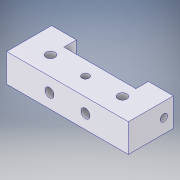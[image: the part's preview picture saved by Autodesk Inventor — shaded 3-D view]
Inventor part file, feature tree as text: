
AUTODESK INVENTOR PART (.ipt)
format: ipt  version: 2017 (Build 210142000, 142)  size: 185,344 bytes
history: native  units: in
note: dims shown in document units (in); Inventor stores cm internally (conversion verified against a paired STEP export)
features: extrude x8, sketch x8, projected_geometry x5
ambient origin geometry x8: Origin, YZ Plane, XZ Plane, XY Plane, X Axis, Y Axis, Z Axis, Center Point
bodies: Solid1 (feature_tree)
feature tree (21):
  extrude  "Extrusion1"  Depth=1.6929in
  extrude  "Extrusion2"  Depth=0.3937in
  extrude  "Extrusion3"  Depth=0.1969in TaperAngle=0.0deg
  extrude  "Extrusion4"  Depth=0.1969in
  extrude  "Extrusion5"  Depth=0.0984in
  extrude  "Extrusion6"  Depth=0.3937in TaperAngle=0.0deg
  extrude  "Extrusion7"  Depth=1.0in
  extrude  "Extrusion8"  Depth=0.625in
  sketch  "Sketch1"  dims[d0=2.4016in d1=1.6929in]
  sketch  "Sketch2"  dims[d2=0.3937in d3=0.0in d4=0.4921in]
  sketch  "Sketch3"  dims[d5=0.0984in d6=0.1969in d7=0.0in]
  projected_geometry  "Projected Loop1"
  sketch  "Sketch4"  dims[d8=0.1969in d9=0.0in d10=0.25in]
  sketch  "Sketch5"  dims[d11=0.25in d12=0.0984in]
  projected_geometry  "Projected Loop2"
  sketch  "Sketch6"  dims[d13=0.0984in d14=0.3937in d15=0.0in]
  projected_geometry  "Projected Loop3"
  sketch  "Sketch7"  dims[d16=1.0in d17=1.5in]
  projected_geometry  "Projected Loop4"
  sketch  "Sketch8"  dims[d18=0.3937in d19=0.0in d20=0.625in d21=1.0in d22=0.0in d23=0.5in d24=0.263in d25=0.125in d26=1.0in d27=0.0in d28=0.25in d29=0.125in d30=0.25in d31=0.125in d32=0.125in d33=0.0in]
  projected_geometry  "Projected Loop5"
